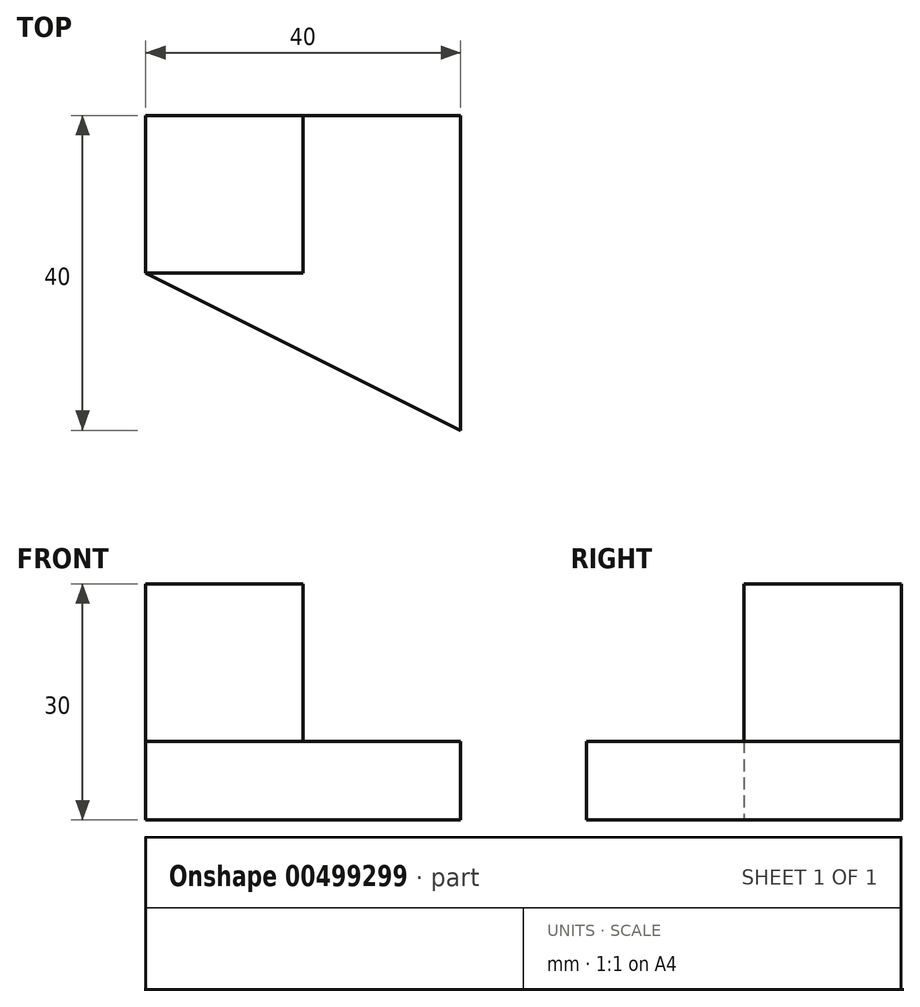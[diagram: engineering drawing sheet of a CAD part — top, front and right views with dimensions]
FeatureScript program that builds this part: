
annotation { "Feature Type Name" : "Feature", "Feature Type Description" : "" }
export const myFeature = defineFeature(function(context is Context, id is Id, definition is map)
    precondition{}
    {
        {
            var Q0;
            Q0=qCreatedBy(makeId("Top.planeOp"),FACE);
            var sketch = newSketch(context, id + "F0", { "sketchPlane" : qUnion([Q0])});
            skLineSegment(sketch, "E0", {"start": v(-31.6, 9.4) * mm, "end": v(-31.6, -10.6) * mm});
            skLineSegment(sketch, "E1", {"start": v(-31.6, 9.4) * mm, "end": v(8.4, 9.4) * mm});
            skLineSegment(sketch, "E2", {"start": v(8.4, 9.4) * mm, "end": v(8.4, -30.6) * mm});
            skLineSegment(sketch, "E3", {"start": v(-31.6, -10.6) * mm, "end": v(8.4, -30.6) * mm});
            skLineSegment(sketch, "E4", {"start": v(-31.6, -10.6) * mm, "end": v(-11.6, -10.6) * mm});
            skLineSegment(sketch, "E5", {"start": v(-11.6, 9.4) * mm, "end": v(-11.6, -10.6) * mm});
            skSolve(sketch);
        }
        {
            var Q0;
            {var subQ0=sQuery(id+"F0.wireOp",EDGE,"E2");Q0=makeQuery(id+"F0.imprint","IMPRINT",FACE,{"disambiguationData":[TD([[makeQuery(id+"F0.imprint","IMPRINT",EDGE,{"derivedFrom":subQ0}),-1.0]])]});}
            var Q1;
            {var subQ0=sQuery(id+"F0.wireOp",EDGE,"E0");Q1=makeQuery(id+"F0.imprint","IMPRINT",FACE,{"disambiguationData":[TD([[makeQuery(id+"F0.imprint","IMPRINT",EDGE,{"derivedFrom":subQ0}),1.0]])]});}
            extrude(context, id + "F1", {"entities" : qUnion([Q0, Q1]), "depth" : 10 * mm});
        }
        {
            var Q0;
            Q0=makeQuery(id+"F1.opExtrude","CAP_FACE",FACE,{"disambiguationData":[OSD([sQuery(id+"F0.wireOp",EDGE,"E0"),sQuery(id+"F0.wireOp",EDGE,"E1"),sQuery(id+"F0.wireOp",EDGE,"E2"),sQuery(id+"F0.wireOp",EDGE,"E3")])],"isStart":false});
            var sketch = newSketch(context, id + "F2", { "sketchPlane" : qUnion([Q0])});
            skLineSegment(sketch, "E6", {"start": v(-31.6, 9.4) * mm, "end": v(-31.6, -10.6) * mm});
            skLineSegment(sketch, "E7", {"start": v(-31.6, -10.6) * mm, "end": v(-11.6, -10.6) * mm});
            skLineSegment(sketch, "E8", {"start": v(-11.6, 9.4) * mm, "end": v(-11.6, -10.6) * mm});
            skLineSegment(sketch, "E9", {"start": v(-11.6, 9.4) * mm, "end": v(-31.6, 9.4) * mm});
            skSolve(sketch);
        }
        {
            var Q0;
            Q0=makeQuery(id+"F2.imprint","IMPRINT",FACE,{"disambiguationData":[TD([[makeQuery(id+"F2.imprint","IMPRINT",EDGE,{"derivedFrom":sQuery(id+"F2.wireOp",EDGE,"E6")}),1.0]])]});
            extrude(context, id + "F3", {"entities" : qUnion([Q0]), "operationType" : NewBodyOperationType.ADD, "depth" : 20 * mm});
        }
    });
